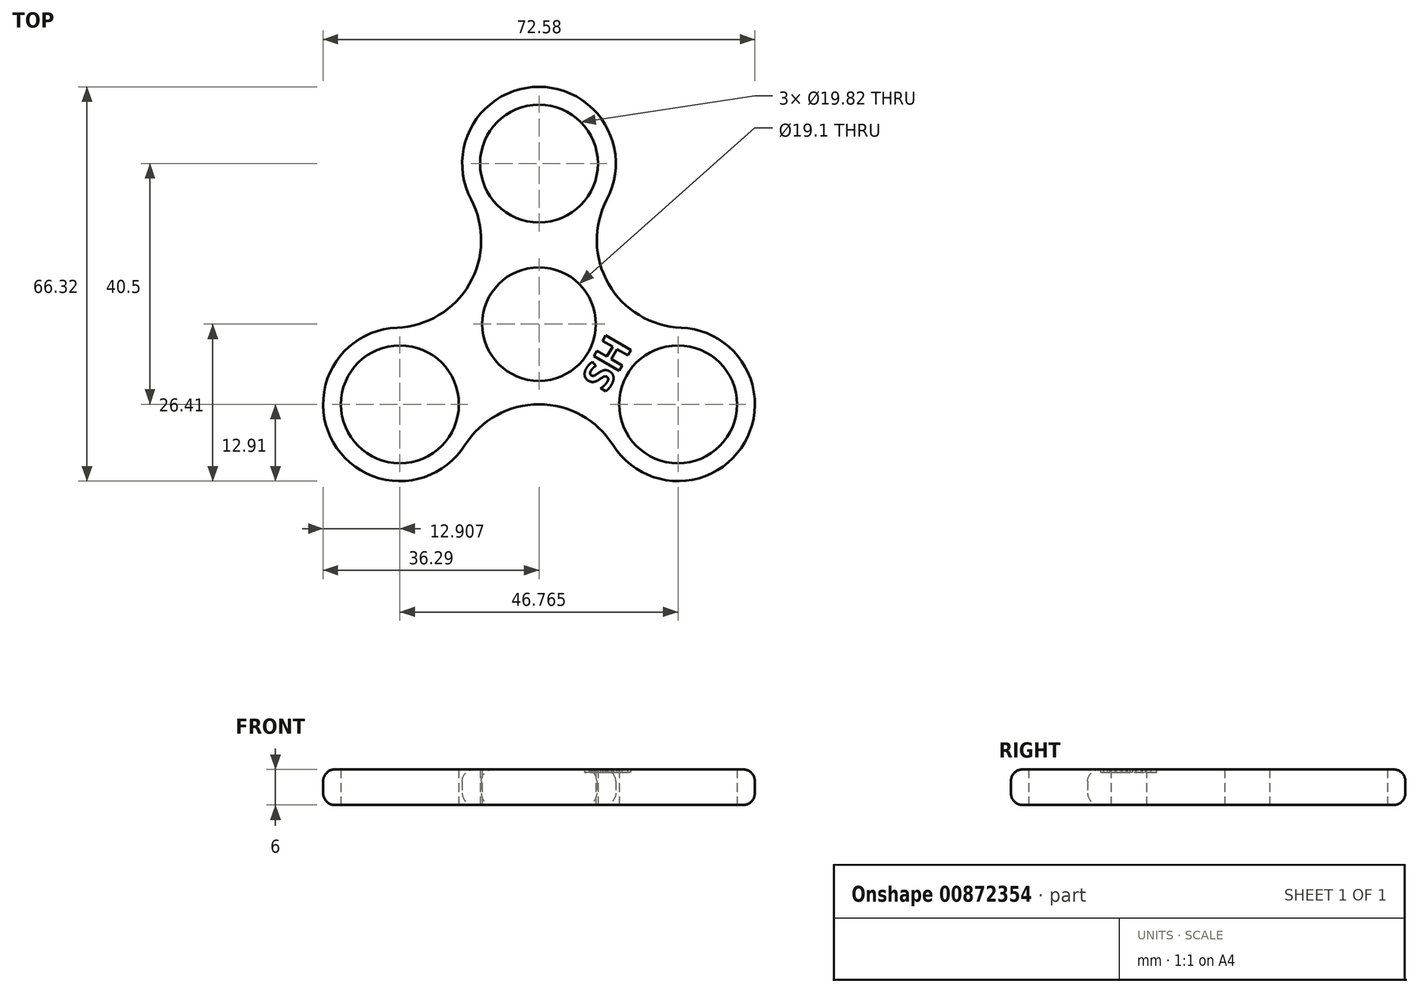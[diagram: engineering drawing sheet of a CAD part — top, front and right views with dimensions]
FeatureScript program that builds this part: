
annotation { "Feature Type Name" : "Feature", "Feature Type Description" : "" }
export const myFeature = defineFeature(function(context is Context, id is Id, definition is map)
    precondition{}
    {
        {
            var Q0;
            Q0=qCreatedBy(makeId("Top.planeOp"),FACE);
            var sketch = newSketch(context, id + "F0", { "sketchPlane" : qUnion([Q0])});
            skCircle(sketch, "E0", {"center": v(0, 0) * mm, "radius": 9.55 * mm});
            skCircle(sketch, "E1", {"center": v(0, 27) * mm, "radius": 9.9 * mm});
            skArc(sketch, "E2.0", {"start": v(11.42, 20.98) * mm, "mid": v(0, 39.91) * mm, "end": v(-11.42, 20.98) * mm});
            skCircle(sketch, "E3.1.0", {"center": v(-23.38, -13.5) * mm, "radius": 9.9 * mm});
            skArc(sketch, "E3.1.1", {"start": v(-23.88, -0.6) * mm, "mid": v(-34.56, -19.95) * mm, "end": v(-12.46, -20.38) * mm});
            skCircle(sketch, "E3.2.0", {"center": v(23.38, -13.5) * mm, "radius": 9.9 * mm});
            skArc(sketch, "E3.2.1", {"start": v(12.46, -20.38) * mm, "mid": v(34.56, -19.95) * mm, "end": v(23.88, -0.6) * mm});
            skLineSegment(sketch, "E4", {"start": v(-23.38, -13.5) * mm, "end": v(51.3, 29.62) * mm, "construction": true});
            skLineSegment(sketch, "E5", {"start": v(23.38, -13.5) * mm, "end": v(0, 27) * mm, "construction": true});
            skArc(sketch, "E6", {"start": v(11.42, 20.98) * mm, "mid": v(11.7, 6.75) * mm, "end": v(23.88, -0.6) * mm});
            skArc(sketch, "E7.1.0", {"start": v(-23.88, -0.6) * mm, "mid": v(-11.7, 6.75) * mm, "end": v(-11.42, 20.98) * mm});
            skArc(sketch, "E7.2.0", {"start": v(12.46, -20.38) * mm, "mid": v(0, -13.5) * mm, "end": v(-12.46, -20.38) * mm});
            skLineSegment(sketch, "E8", {"start": v(0, 0) * mm, "end": v(23.38, -13.5) * mm, "construction": true});
            skSolve(sketch);
        }
        {
            var Q0;
            Q0=makeQuery(id+"F0.imprint","IMPRINT",FACE,{"disambiguationData":[TD([[makeQuery(id+"F0.imprint","IMPRINT",EDGE,{"derivedFrom":sQuery(id+"F0.wireOp",EDGE,"E0")}),-1.0]])]});
            extrude(context, id + "F1", {"entities" : qUnion([Q0]), "depth" : 6 * mm, "offsetDistance" : 25 * mm});
        }
        {
            var Q0;
            Q0=makeQuery(id+"F1.opExtrude","CAP_EDGE",EDGE,{"disambiguationData":[OSD([sQuery(id+"F0.wireOp",EDGE,"E7.2.0")])],"isStart":false});
            var Q1;
            Q1=makeQuery(id+"F1.opExtrude","CAP_EDGE",EDGE,{"disambiguationData":[OSD([sQuery(id+"F0.wireOp",EDGE,"E7.2.0")])],"isStart":true});
            fillet(context, id + "F2", {"entities" : qUnion([Q0, Q1]), "radius" : 2 * mm, "tangentPropagation" : true, "allowEdgeOverflow" : false});
        }
        {
            var Q0;
            Q0=makeQuery(id+"F1.opExtrude","CAP_FACE",FACE,{"disambiguationData":[OSD([sQuery(id+"F0.wireOp",EDGE,"E0"),sQuery(id+"F0.wireOp",EDGE,"E1"),sQuery(id+"F0.wireOp",EDGE,"E2.0"),sQuery(id+"F0.wireOp",EDGE,"E3.1.0"),sQuery(id+"F0.wireOp",EDGE,"E3.1.1"),sQuery(id+"F0.wireOp",EDGE,"E3.2.0"),sQuery(id+"F0.wireOp",EDGE,"E3.2.1"),sQuery(id+"F0.wireOp",EDGE,"E6"),sQuery(id+"F0.wireOp",EDGE,"E7.1.0"),sQuery(id+"F0.wireOp",EDGE,"E7.2.0")])],"isStart":false});
            var sketch = newSketch(context, id + "F3", { "sketchPlane" : qUnion([Q0])});
            skPoint(sketch, "E9.0", {"position": v(0, 0) * mm});
            skPoint(sketch, "E10.0", {"position": v(32.83, -18.96) * mm});
            skText(sketch, "E11", { "text": "SH", "fontName": "OpenSans-Bold.ttf"});
            skLineSegment(sketch, "E12", {"start": v(0, 0) * mm, "end": v(23.38, -13.5) * mm, "construction": true});
            skLineSegment(sketch, "E13", {"start": v(8.27, -4.77) * mm, "end": v(14.8, -8.54) * mm, "construction": true});
            const initialGuessF3  = {"E11": [0.01127, -0.01167, 0.5, 0.86603, 0.00495]};
            skSetInitialGuess(sketch, initialGuessF3);
            skSolve(sketch);
        }
        {
            var Q0;
            Q0=qSketchRegion(id+"F3",true);
            extrude(context, id + "F4", {"entities" : qUnion([Q0]), "operationType" : NewBodyOperationType.REMOVE, "oppositeDirection" : true, "depth" : 0.5 * mm, "offsetDistance" : 25 * mm});
        }
    });
